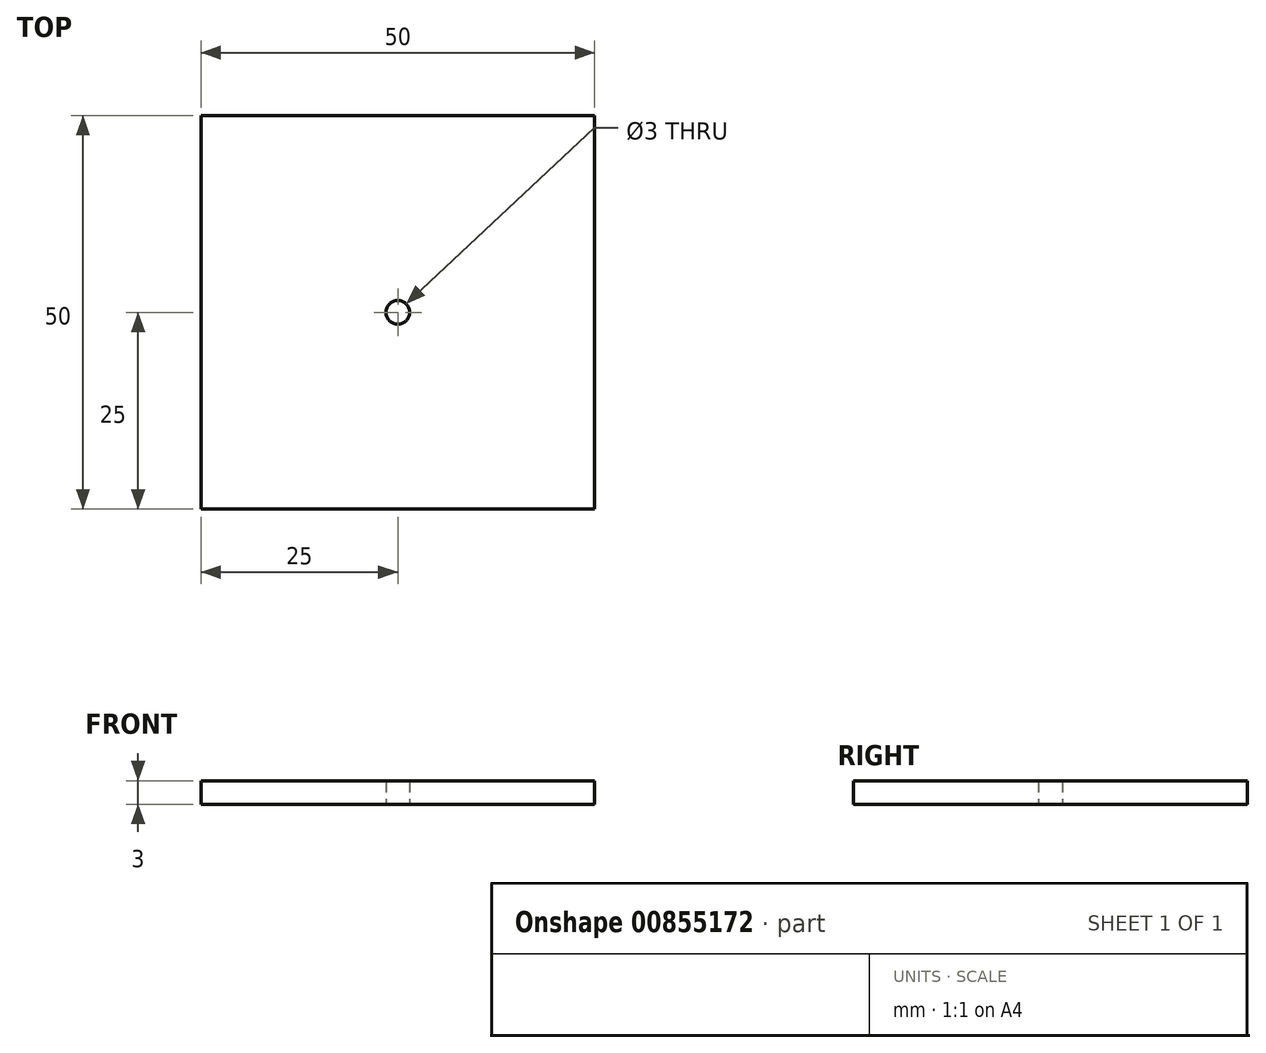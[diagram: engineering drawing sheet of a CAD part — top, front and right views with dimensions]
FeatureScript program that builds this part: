
annotation { "Feature Type Name" : "Feature", "Feature Type Description" : "" }
export const myFeature = defineFeature(function(context is Context, id is Id, definition is map)
    precondition{}
    {
        {
            var Q0;
            Q0=qCreatedBy(makeId("Top.planeOp"),FACE);
            var sketch = newSketch(context, id + "F0", { "sketchPlane" : qUnion([Q0])});
            skLineSegment(sketch, "E0.bottom", {"start": v(25, -25) * mm, "end": v(-25, -25) * mm});
            skLineSegment(sketch, "E0.top", {"start": v(25, 25) * mm, "end": v(-25, 25) * mm});
            skLineSegment(sketch, "E0.left", {"start": v(25, -25) * mm, "end": v(25, 25) * mm});
            skLineSegment(sketch, "E0.right", {"start": v(-25, -25) * mm, "end": v(-25, 25) * mm});
            skPoint(sketch, "E0.middle", {"position": v(0, 0) * mm});
            skCircle(sketch, "E1", {"center": v(0, 0) * mm, "radius": 1.5 * mm});
            skSolve(sketch);
        }
        {
            var Q0;
            Q0=makeQuery(id+"F0.imprint","IMPRINT",FACE,{"disambiguationData":[TD([[makeQuery(id+"F0.imprint","IMPRINT",EDGE,{"derivedFrom":sQuery(id+"F0.wireOp",EDGE,"E0.bottom")}),-1.0]])]});
            extrude(context, id + "F1", {"entities" : qUnion([Q0]), "depth" : 3 * mm, "offsetDistance" : 25 * mm});
        }
    });
